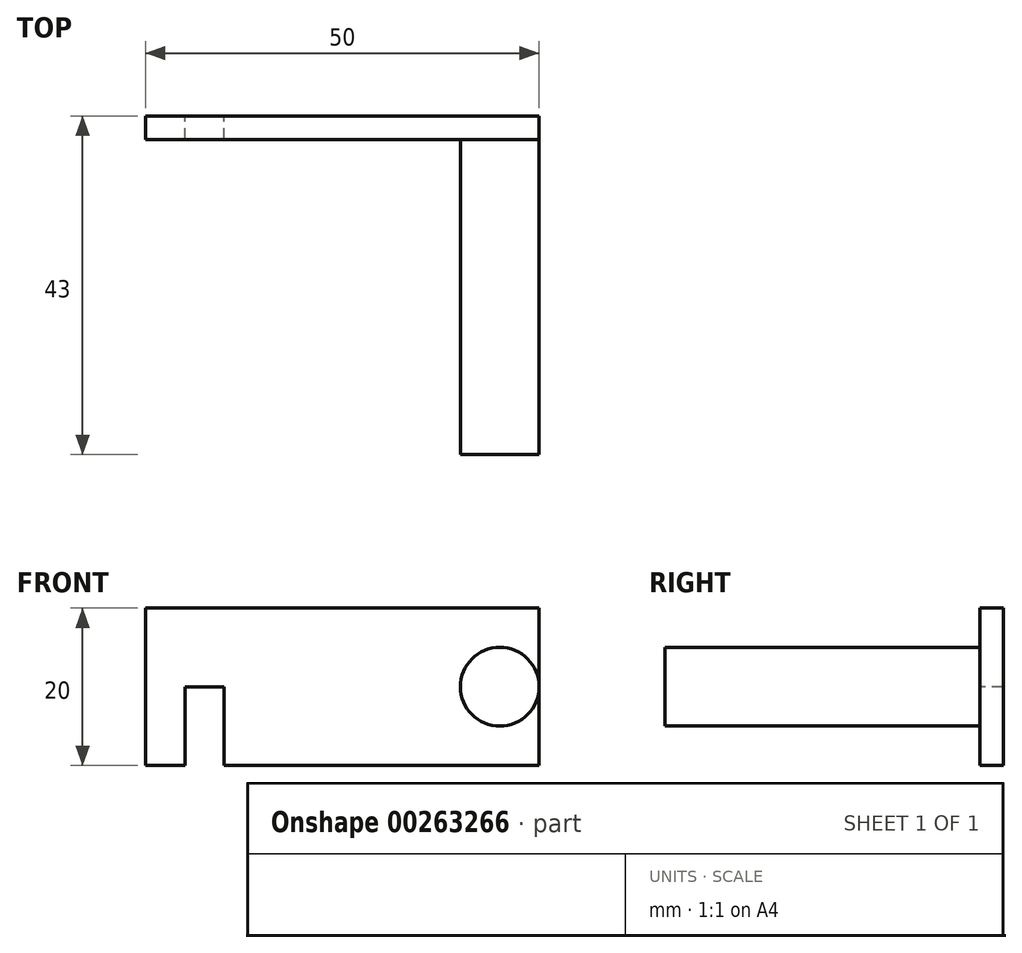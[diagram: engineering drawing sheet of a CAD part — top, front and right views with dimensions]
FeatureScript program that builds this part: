
annotation { "Feature Type Name" : "Feature", "Feature Type Description" : "" }
export const myFeature = defineFeature(function(context is Context, id is Id, definition is map)
    precondition{}
    {
        {
            var Q0;
            Q0=qCreatedBy(makeId("Front.planeOp"),FACE);
            var sketch = newSketch(context, id + "F0", { "sketchPlane" : qUnion([Q0])});
            skLineSegment(sketch, "E0.bottom", {"start": v(25, -10) * mm, "end": v(-25, -10) * mm});
            skLineSegment(sketch, "E0.top", {"start": v(25, 10) * mm, "end": v(-25, 10) * mm});
            skLineSegment(sketch, "E0.left", {"start": v(25, -10) * mm, "end": v(25, 10) * mm});
            skLineSegment(sketch, "E0.right", {"start": v(-25, -10) * mm, "end": v(-25, 10) * mm});
            skPoint(sketch, "E0.middle", {"position": v(0, 0) * mm});
            skSolve(sketch);
        }
        {
            var Q0;
            Q0 = qSketchRegion(id + "F0", true);
            extrude(context, id + "F1", {"entities" : qUnion([Q0]), "depth" : 3 * mm});
        }
        {
            var Q0;
            Q0=makeQuery(id+"F1.opExtrude","CAP_FACE",FACE,{"disambiguationData":[OSD([sQuery(id+"F0.wireOp",EDGE,"E0.bottom"),sQuery(id+"F0.wireOp",EDGE,"E0.top"),sQuery(id+"F0.wireOp",EDGE,"E0.left"),sQuery(id+"F0.wireOp",EDGE,"E0.right")])],"isStart":false});
            var sketch = newSketch(context, id + "F2", { "sketchPlane" : qUnion([Q0])});
            skCircle(sketch, "E1", {"center": v(20, 0) * mm, "radius": 5 * mm});
            skSolve(sketch);
        }
        {
            var Q0;
            Q0 = qSketchRegion(id + "F2", true);
            extrude(context, id + "F3", {"entities" : qUnion([Q0]), "operationType" : NewBodyOperationType.ADD, "depth" : 40 * mm});
        }
        {
            var Q0;
            Q0=makeQuery(id+"F1.opExtrude","CAP_FACE",FACE,{"disambiguationData":[OSD([sQuery(id+"F0.wireOp",EDGE,"E0.bottom"),sQuery(id+"F0.wireOp",EDGE,"E0.top"),sQuery(id+"F0.wireOp",EDGE,"E0.left"),sQuery(id+"F0.wireOp",EDGE,"E0.right")])],"isStart":false});
            var sketch = newSketch(context, id + "F4", { "sketchPlane" : qUnion([Q0])});
            skLineSegment(sketch, "E2.bottom", {"start": v(-15, 0) * mm, "end": v(-20, 0) * mm});
            skLineSegment(sketch, "E2.top", {"start": v(-15, -10.3) * mm, "end": v(-20, -10.3) * mm});
            skLineSegment(sketch, "E2.left", {"start": v(-15, 0) * mm, "end": v(-15, -10.3) * mm});
            skLineSegment(sketch, "E2.right", {"start": v(-20, 0) * mm, "end": v(-20, -10.3) * mm});
            skSolve(sketch);
        }
        {
            var Q0;
            Q0 = qSketchRegion(id + "F4", true);
            extrude(context, id + "F5", {"entities" : qUnion([Q0]), "operationType" : NewBodyOperationType.REMOVE, "endBound" : BoundingType.THROUGH_ALL, "oppositeDirection" : true, "depth" : 25 * mm});
        }
    });
